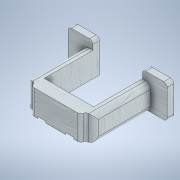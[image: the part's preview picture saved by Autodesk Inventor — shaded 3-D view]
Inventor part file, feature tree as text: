
AUTODESK INVENTOR PART (.ipt)
format: ipt  version: 2021 (Build 250183000, 183)  size: 215,040 bytes
history: native  units: mm
features: extrude x6, sketch x6, fillet x3
ambient origin geometry x8: Origin, YZ Plane, XZ Plane, XY Plane, X Axis, Y Axis, Z Axis, Center Point
bodies: Solid1 (feature_tree)
feature tree (15):
  extrude  "Extrusion1"  Depth=15.0mm
  extrude  "Extrusion2"  Depth=30.0mm
  fillet  "Fillet1"  Radius=15.0mm
  extrude  "Extrusion3"  Depth=3.0mm TaperAngle=0.0deg
  extrude  "Extrusion4"  Depth=5.0mm
  fillet  "Fillet2"  Radius=5.0mm
  fillet  "Fillet3"  Radius=33.5mm
  extrude  "Extrusion5"  Depth=20.0mm
  extrude  "Extrusion6"  Depth=4.0mm TaperAngle=0.0deg
  sketch  "Sketch1"  dims[d0=40.0mm d1=15.0mm]
  sketch  "Sketch2"  dims[d2=5.0mm d3=0.0mm d4=30.0mm d5=15.0mm]
  sketch  "Sketch3"  dims[d6=5.0mm d7=3.0mm d8=0.0mm]
  sketch  "Sketch4"  dims[d9=2.0mm d10=5.0mm d11=5.0mm d12=33.5mm d13=0.0mm]
  sketch  "Sketch5"  dims[d18=15.0mm d19=20.0mm]
  sketch  "Sketch6"  dims[d20=15.0mm d21=4.0mm d22=0.0mm d23=3.0mm d24=2.0mm d25=1.0mm d26=0.0mm d27=1.5mm d28=1.5mm d29=10.0mm d30=0.0mm]
